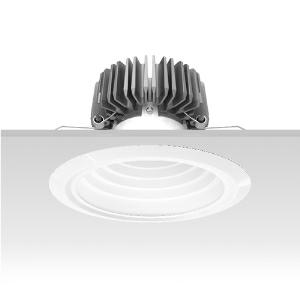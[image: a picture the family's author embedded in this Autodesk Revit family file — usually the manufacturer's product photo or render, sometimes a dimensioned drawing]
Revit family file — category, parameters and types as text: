
# Revit family: 3f_filippi_-_3f_reno_bianco_ampio_3f_filippi_-_30633_a01025_-_3f_reno_200_wh_3000-930_wide___vt_wh_4fba
name_source: partatom
category: Lighting Fixtures
units: mm (PartAtom-declared; Revit-internal decimal feet)

## family parameters
Cut with Voids When Loaded = No
Host = Face
Light Source = No
Part Type = Normal
Room Calculation Point = No
Round Connector Dimension = Use Diameter
Shared = No

## types (1)
- 3F Filippi - 3F Reno Bianco Ampio (1 x LED, 2537 lm, 37 W, 3000 K)
    Apparent Load = 37 VA
    Approval mark = CE
    CIE Flux Codes = 75 94 99 100 100
    Color Rendering = 90
    Color Temperature = 3000 K
    Control Gear = Electronic ballast
    Default Elevation = 1800 mm
    Description = ILLUMINOTECHNICAL
Luminous efficiency 100% (DLOR 100%, ULOR 0%).
Initial luminous flux of the luminaire 2537 lm.
Direct symmetric wide distribution.
Installation Interdistance Transv.D = 1.56 x hu - Long.D = 1.56 x hu.
Tabular UGR (CIE 117 - 4H-8H; S=0.25H; 70/50/20): RUG 21.8 - 21.7.
Beam angle: 74° - 74°.
Luminous efficacy 69 lm/W.
Lifetime (L90/B10): 30000 h. (tq+25°C)
Lifetime (L85/B10): 50000 h. (tq+25°C)
Lifetime (L70/B10): 80000 h. (tq+25°C)
Sudden decreased luminous flux after 50000 hours: 0% (C0).
Photobiological safety in compliance with IEC/TR 62778: RG0 risk exempt, (IEC 62471).
In compliance with IEC/EN 62722-2-1 - IEC/EN 62717 standards.

SOURCE
Compact LED module 3000/930.
Energy efficiency class (UE 2019/2020 - UE 2019/2015): E.
CIE 13.3 Colour rendering index: CRI >90 (R9 >50%).
IES TM-30 Fidelity Index: Rf = 92 Rg = 101.
CCT nominal colour temperature 3000 K.
Colour initial tolerance (MacAdam): SDCM 3.
Zhaga Book 3 compliant.

MECHANICAL
Passive heat dissipator in die-casting aluminium, oversized, for optimum thermal management of the LED module.
Parabolic element with graduated/concentric rings in white polycarbonate.
Transparent external lens with glossy and satin differentiated surfaces, with a cooling and anti-insect system in methacrylate (PMMA).
Fastening spring clips in stainless steel.
Dimensions: diameter 226 mm, height 146 mm. Weight 1.705 kg.
IP44 protection degree for exposed part, IP20 for recessed part.
Mechanical strength to impacts IK06 (1 joule).
Glow-wire test resistance 650°C.

ELECTRICAL
Wiring on a separate unit.
Halogen Free electronic wiring 230V-50/60Hz, power factor 0.95, THD <25%, constant output current, SELV, class II, 1 driver.
Power of the luminaire 37 W.
ENEC - CE.
SAFE FLICKER: PstLM=<1 and SVM=<0.4 (IEC TR 61547-1 and IEC TR 63158), to ensure a more comfortable and safe light.
Luminaire compliant with EN 60598-2-22 for power supply from a centralised emergency system CPSS (Central Power Supply System), not incorporated in the luminaire - high risk areas excluded. The default power and flux are 100% in AC and 100% in DC.
Ambient temperature from 0°C to +25°C.
Temperature class T6 max 85°C.
Relative humidity UR: <85%.

INSTALLATION
Pull-up recessed fitting.
False ceiling carving: 200 mm.
All accessories dedicated to this product are available on the Catalog and on our website www.3F-Filippi.com.

ACCESSORIES
A01025 - VT transparent glass, tempered, not flammable, locked and in line with the trim, in white polycarbonate.

APPLICATIONS
Environments: architectural, commercial, exhibition areas, transit areas, corridors, shops, display windows, service areas.
In false ceilings with narrow voids.

WARNING
Luminaire designed for disposal/recycling at end-of-life.
Replaceable (LED only) light source by a professional. Replaceable control gear by a professional.
    Height = 0 mm  [stored 0 ft]
    Lamp = 1 x LED
    Lamp Light Flux = 2537 lm
    Lamp Power = 37 W
    Lamp count = 1
    Length = 226 mm
    Lifetime = 50000 h
    Luminous efficacy = 69 lm/W
    Manufacturer = 3F Filippi
    ModVariant = No
    Model = 3F Filippi - 30633+A01025 - 3F Reno 200 WH 3000-930 WIDE + VT WH
    Mounting Place = Ceiling
    Mounting Type = Recessed
    Number of Poles = 1
    OnlyDefault = Yes
    Power Factor = 1
    Product Name = 3F Filippi - 3F Reno Bianco Ampio
    Product group = recessed luminaire
    ProductGroupID = 4
    Protection Class = Protection class II
    Protection Degree = IP 20
    RLX_Detail_Level = 1
    RLX_Emergency_Light_Flux = 0 lm
    RLX_Emergency_Type = 0
    RLX_Emergency_Type_DB = No
    RlxData = <blob elided: 95509 chars, md5=f8b0222e>
    Socket = socket
    Standby Power = 0 W
    System Light Flux = 2537 lm
    System Power = 37 W
    Type Comments = Product without accessories
    Type Image = 3ffilippi_3f_reno_200_wh__a01025.jpg
    URL = http://relux.com
    VarID = ---
    Voltage = 0 V
    Weight = 0.00 kg
    Width = 0 mm  [stored 0 ft]

note: [stored X ft] marks values corroborated as IEEE doubles in the binary element streams (Revit-internal decimal feet)

## geometry (parser evidence)
native form markers: Blend x4, Sweep x11
no freeform markers — native parametric forms only
